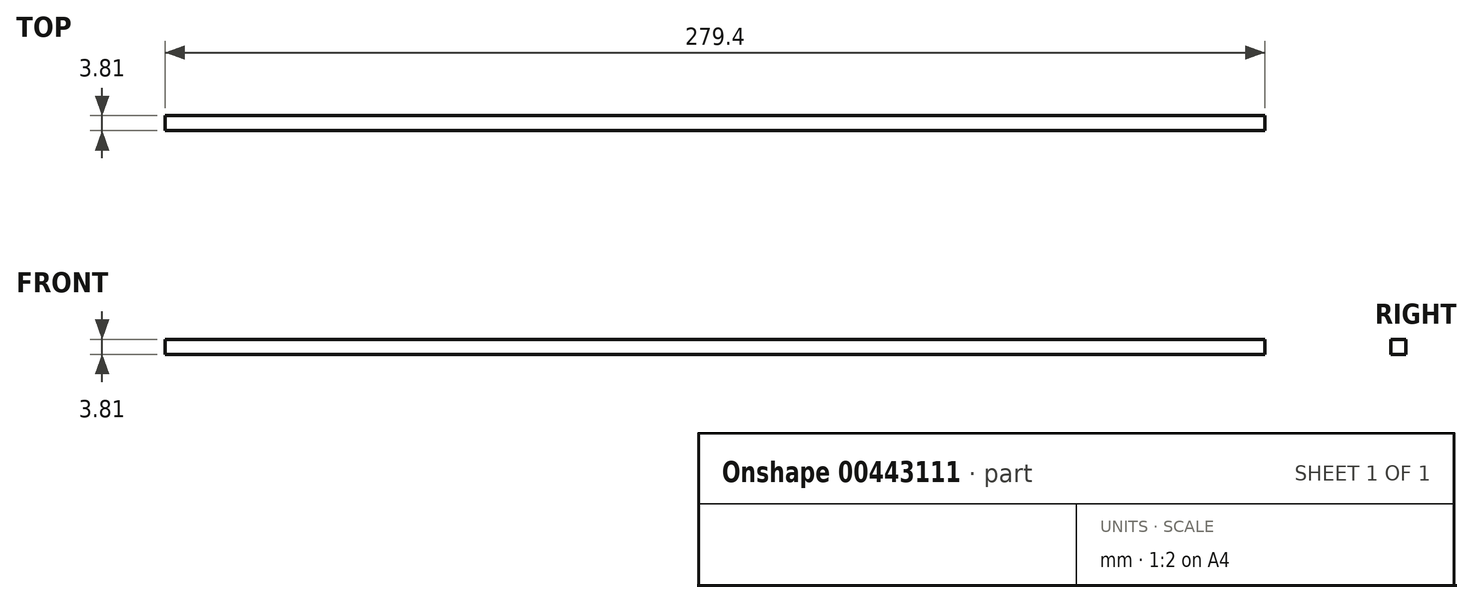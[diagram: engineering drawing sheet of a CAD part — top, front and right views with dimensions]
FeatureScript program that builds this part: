
annotation { "Feature Type Name" : "Feature", "Feature Type Description" : "" }
export const myFeature = defineFeature(function(context is Context, id is Id, definition is map)
    precondition{}
    {
        {
            var Q0;
            Q0=qCreatedBy(makeId("Front.planeOp"),FACE);
            var sketch = newSketch(context, id + "F0", { "sketchPlane" : qUnion([Q0])});
            skLineSegment(sketch, "E0.bottom", {"start": v(-141.71, -89.04) * mm, "end": v(137.69, -89.04) * mm});
            skLineSegment(sketch, "E0.top", {"start": v(-141.71, -92.85) * mm, "end": v(137.69, -92.85) * mm});
            skLineSegment(sketch, "E0.left", {"start": v(-141.71, -89.04) * mm, "end": v(-141.71, -92.85) * mm});
            skLineSegment(sketch, "E0.right", {"start": v(137.69, -89.04) * mm, "end": v(137.69, -92.85) * mm});
            skSolve(sketch);
        }
        {
            var Q0;
            Q0=makeQuery(id+"F0.imprint","IMPRINT",FACE,{"disambiguationData":[TD([[makeQuery(id+"F0.imprint","IMPRINT",EDGE,{"derivedFrom":sQuery(id+"F0.wireOp",EDGE,"E0.bottom")}),-1.0]])]});
            extrude(context, id + "F1", {"entities" : qUnion([Q0]), "depth" : 3.8 * mm});
        }
    });
